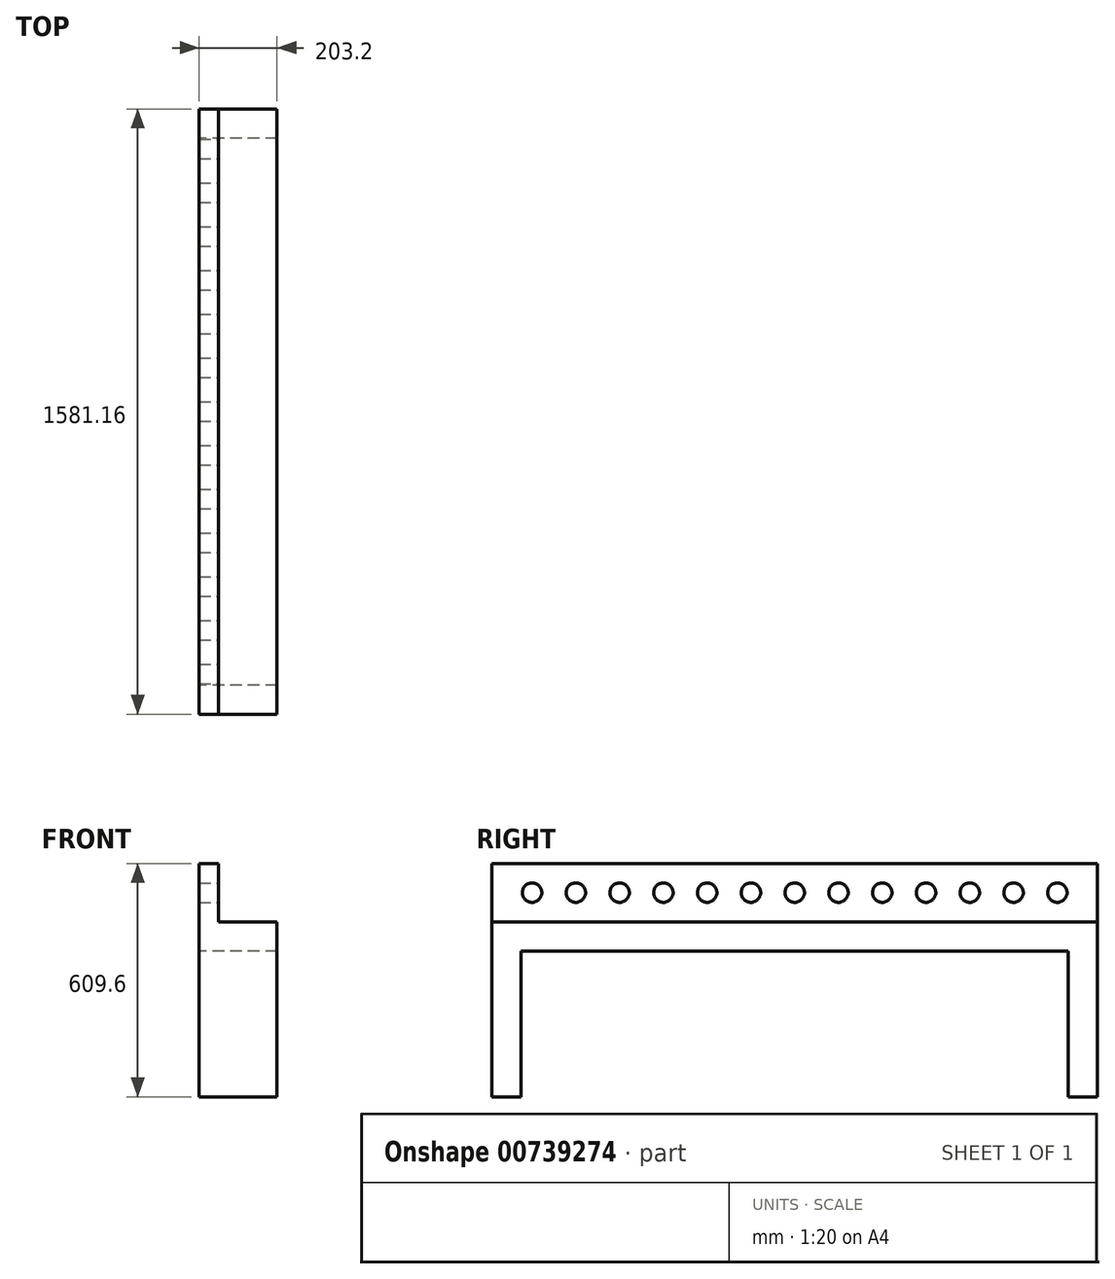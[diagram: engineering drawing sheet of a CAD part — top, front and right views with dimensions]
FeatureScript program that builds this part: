
annotation { "Feature Type Name" : "Feature", "Feature Type Description" : "" }
export const myFeature = defineFeature(function(context is Context, id is Id, definition is map)
    precondition{}
    {
        {
            var Q0;
            Q0=qCreatedBy(makeId("Right.planeOp"),FACE);
            var sketch = newSketch(context, id + "F0", { "sketchPlane" : qUnion([Q0])});
            skLineSegment(sketch, "E0", {"start": v(-790.58, 0) * mm, "end": v(-714.38, 0) * mm});
            skLineSegment(sketch, "E1", {"start": v(-714.38, 0) * mm, "end": v(-714.38, 381) * mm});
            skLineSegment(sketch, "E2", {"start": v(-714.38, 381) * mm, "end": v(714.38, 381) * mm});
            skLineSegment(sketch, "E3", {"start": v(714.38, 381) * mm, "end": v(714.38, 0) * mm});
            skLineSegment(sketch, "E4", {"start": v(714.38, 0) * mm, "end": v(790.58, 0) * mm});
            skLineSegment(sketch, "E5", {"start": v(790.58, 0) * mm, "end": v(790.58, 457.2) * mm});
            skLineSegment(sketch, "E6", {"start": v(790.58, 457.2) * mm, "end": v(-790.58, 457.2) * mm});
            skLineSegment(sketch, "E7", {"start": v(-790.58, 457.2) * mm, "end": v(-790.58, 0) * mm});
            skSolve(sketch);
        }
        {
            var Q0;
            Q0 = qSketchRegion(id + "F0", true);
            extrude(context, id + "F1", {"entities" : qUnion([Q0]), "endBound" : BoundingType.SYMMETRIC, "depth" : 203.2 * mm, "offsetDistance" : 25.4 * mm});
        }
        {
            var Q0;
            Q0=makeQuery(id+"F1.opExtrude","SWEPT_FACE",FACE,{"disambiguationData":[OSD([sQuery(id+"F0.wireOp",EDGE,"E7")])]});
            var sketch = newSketch(context, id + "F2", { "sketchPlane" : qUnion([Q0])});
            skLineSegment(sketch, "E8.bottom", {"start": v(-101.6, 457.2) * mm, "end": v(-50.8, 457.2) * mm});
            skLineSegment(sketch, "E8.top", {"start": v(-101.6, 609.6) * mm, "end": v(-50.8, 609.6) * mm});
            skLineSegment(sketch, "E8.left", {"start": v(-101.6, 457.2) * mm, "end": v(-101.6, 609.6) * mm});
            skLineSegment(sketch, "E8.right", {"start": v(-50.8, 457.2) * mm, "end": v(-50.8, 609.6) * mm});
            skSolve(sketch);
        }
        {
            var Q0;
            Q0 = qSketchRegion(id + "F2", true);
            var Q1;
            Q1=makeQuery(id+"F1.opExtrude","SWEPT_FACE",FACE,{"disambiguationData":[OSD([sQuery(id+"F0.wireOp",EDGE,"E5")])]});
            extrude(context, id + "F3", {"entities" : qUnion([Q0]), "operationType" : NewBodyOperationType.ADD, "endBound" : BoundingType.UP_TO_SURFACE, "oppositeDirection" : true, "depth" : 25.4 * mm, "endBoundEntityFace" : qUnion([Q1]), "offsetDistance" : 25.4 * mm});
        }
        {
            var Q0;
            Q0=makeQuery(id+"F3.opExtrude","SWEPT_FACE",FACE,{"disambiguationData":[OSD([sQuery(id+"F2.wireOp",EDGE,"E8.right")])]});
            var sketch = newSketch(context, id + "F4", { "sketchPlane" : qUnion([Q0])});
            skPoint(sketch, "E9.middle", {"position": v(0, 533.4) * mm});
            skCircle(sketch, "E10", {"center": v(-457.2, 533.4) * mm, "radius": 25.4 * mm});
            skCircle(sketch, "E11", {"center": v(-342.9, 533.4) * mm, "radius": 25.4 * mm});
            skCircle(sketch, "E12", {"center": v(-228.6, 533.4) * mm, "radius": 25.4 * mm});
            skCircle(sketch, "E13", {"center": v(-114.3, 533.4) * mm, "radius": 25.4 * mm});
            skCircle(sketch, "E14", {"center": v(0, 533.4) * mm, "radius": 25.4 * mm});
            skCircle(sketch, "E15", {"center": v(-685.8, 533.4) * mm, "radius": 25.4 * mm});
            skCircle(sketch, "E16", {"center": v(-571.5, 533.4) * mm, "radius": 25.4 * mm});
            skCircle(sketch, "E17.MirrorC", {"center": v(114.3, 533.4) * mm, "radius": 25.4 * mm});
            skCircle(sketch, "E18.MirrorC", {"center": v(228.6, 533.4) * mm, "radius": 25.4 * mm});
            skCircle(sketch, "E19.MirrorC", {"center": v(342.9, 533.4) * mm, "radius": 25.4 * mm});
            skCircle(sketch, "E20.MirrorC", {"center": v(457.2, 533.4) * mm, "radius": 25.4 * mm});
            skCircle(sketch, "E21.MirrorC", {"center": v(571.5, 533.4) * mm, "radius": 25.4 * mm});
            skCircle(sketch, "E22.MirrorC", {"center": v(685.8, 533.4) * mm, "radius": 25.4 * mm});
            skSolve(sketch);
        }
        {
            var Q0;
            Q0 = qSketchRegion(id + "F4", true);
            extrude(context, id + "F5", {"entities" : qUnion([Q0]), "operationType" : NewBodyOperationType.REMOVE, "endBound" : BoundingType.UP_TO_NEXT, "oppositeDirection" : true, "depth" : 25.4 * mm, "offsetDistance" : 25.4 * mm});
        }
    });
